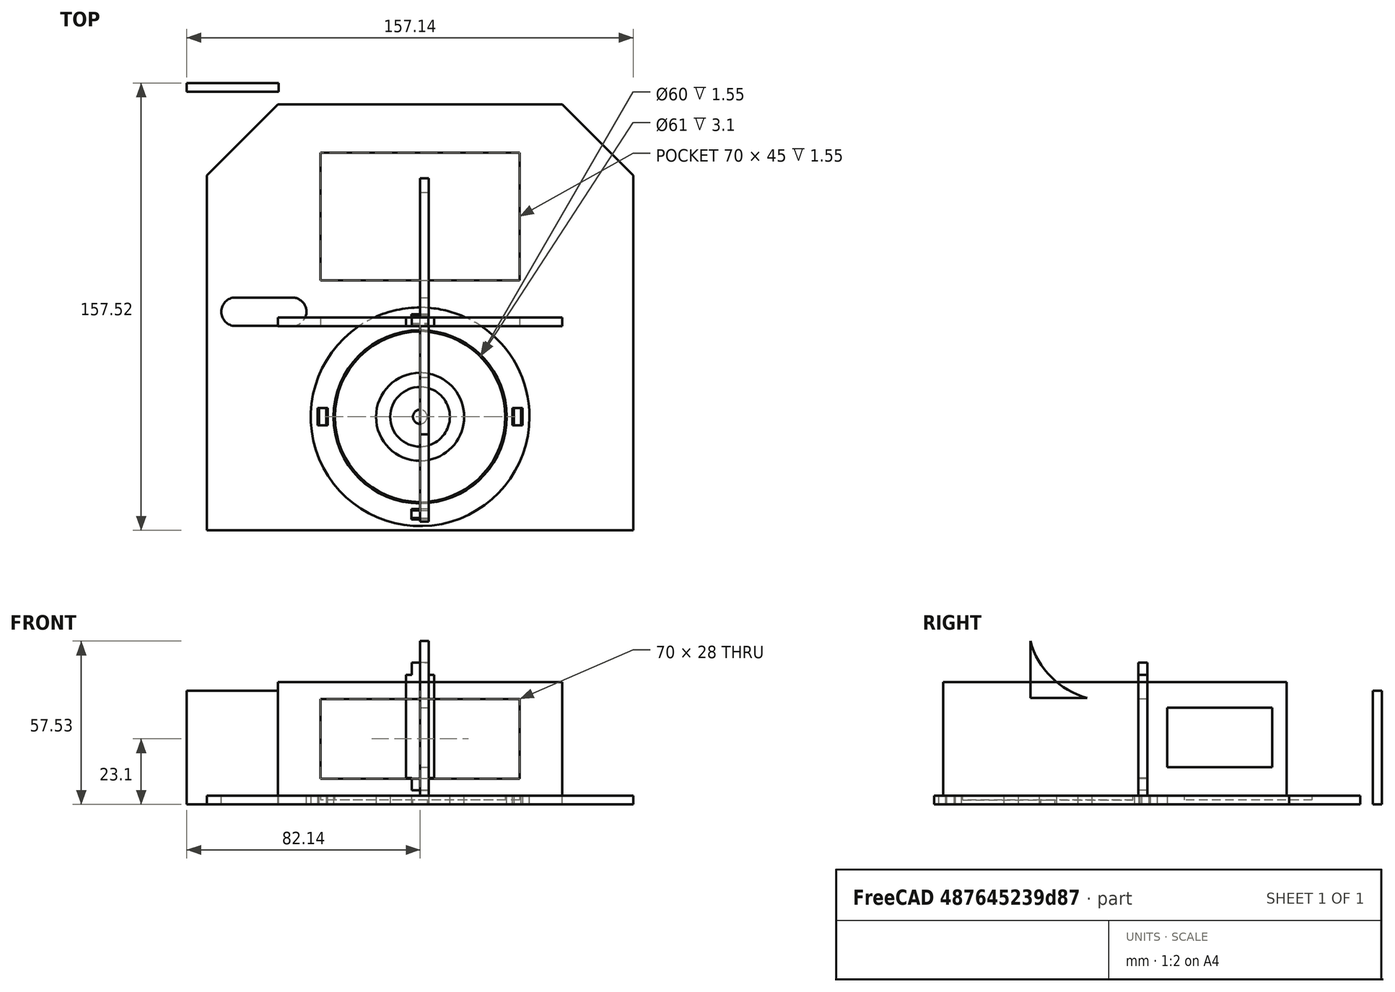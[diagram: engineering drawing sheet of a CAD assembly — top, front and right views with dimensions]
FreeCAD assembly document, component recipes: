
FREECAD ASSEMBLY — COMPONENT RECIPES ("Vehicle_project_3")

This assembly document has 15 components, labeled P0..P14 below (a component is one placed body or linked part). 13 of them carry a construction recipe — the FreeCAD feature program that regenerates the part from scratch, quoted from this document or its linked companion documents; the rest are supplied as boundary geometry only. No exploded tour is included for this assembly.
COMPONENT P0 — geometry summary ("Slice.003"; no construction recipe available for this part):
  bounding box: 150.0 x 105.5 x 72.3 mm
  tessellated surface: 1,640 triangles
  volume: 46763 mm^3 (4% of its bounding box)
COMPONENT P1 — geometry summary ("Slice.002"; no construction recipe available for this part):
  bounding box: 150.0 x 25.0 x 3.1 mm
  tessellated surface: 12 triangles
  volume: 10656 mm^3 (92% of its bounding box)
  symmetry: mirror-symmetric across its z mid-plane
COMPONENT P2 — recipe-attached ("back_side001", modeled in this document).
Construction recipe (the document's own serialized feature program — sketch geometry with constraints, then the solid features built on it; lengths are millimeters unless a unit is written):

FEATURE [Sketcher::SketchObject] Sketch005
  ArcFitTolerance = 1e-06
  AttachmentSupport = -> [XZ_Plane001]
  FullyConstrained = true
  MakeInternals = false
  MapMode = 5
  Placement = pos=(0,0,0) rot=(1,0,0;1.5708rad)
  expr: Constraints[10] = <<dimensions>>.material_thickness
  expr: Constraints[7] = <<dimensions>>.base_width
  expr: Constraints[8] = <<dimensions>>.base_height
  sketch-geometry (4):
    g0: LineSegment StartX=-75 StartY=43.1 StartZ=0 EndX=-75 EndY=3.1 EndZ=0
    g1: LineSegment StartX=-75 StartY=3.1 StartZ=0 EndX=75 EndY=3.1 EndZ=0
    g2: LineSegment StartX=75 StartY=3.1 StartZ=0 EndX=75 EndY=43.1 EndZ=0
    g3: LineSegment StartX=75 StartY=43.1 StartZ=0 EndX=-75 EndY=43.1 EndZ=0
  constraints (11):
    c: Vertical(g0)
    c: Coincident(g0,g1)
    c: Horizontal(g1)
    c: Coincident(g1,g2)
    c: Coincident(g2,g3)
    c: Coincident(g3,g0)
    c: Vertical(g2)
    c: DistanceX(g3,g3) = 150
    c: DistanceY(g2,g2) = 40
    c: Symmetric(g0,g2,g-2)
    c: Distance(g-1,g1) = 3.1
FEATURE [PartDesign::Pad] Pad001
  Direction = (0,-1,2e-16)
  Length = 3.1
  Length2 = 10
  Placement = pos=(0,0,0) rot=(1,0,0;1.5708rad)
  Profile = -> Sketch005
  ReferenceAxis = -> Sketch005 [N_Axis]
  Refine = true
  Suppressed = false
  Type = 0
  expr: Length = <<dimensions>>.material_thickness
FEATURE [Sketcher::SketchObject] Sketch006
  ArcFitTolerance = 1e-06
  AttachmentSupport = -> [Pad001]
  ExternalGeometry = -> [Pad001]
  FullyConstrained = true
  MakeInternals = false
  MapMode = 5
  Placement = pos=(0,-3.1,0) rot=(1,0,0;1.5708rad)
  expr: Constraints[8] = <<dimensions>>.material_thickness + 5 mm
  sketch-geometry (4):
    g0: LineSegment StartX=-66.9 StartY=18.1 StartZ=0 EndX=-66.9 EndY=6.1 EndZ=0
    g1: LineSegment StartX=-66.9 StartY=6.1 StartZ=0 EndX=-51.9 EndY=6.1 EndZ=0
    g2: LineSegment StartX=-51.9 StartY=6.1 StartZ=0 EndX=-51.9 EndY=18.1 EndZ=0
    g3: LineSegment StartX=-51.9 StartY=18.1 StartZ=0 EndX=-66.9 EndY=18.1 EndZ=0
  constraints (12):
    c: Coincident(g0,g1)
    c: Horizontal(g1)
    c: Coincident(g1,g2)
    c: Coincident(g2,g3)
    c: Coincident(g3,g0)
    c: Horizontal(g3)
    c: Vertical(g2)
    c: Vertical(g0)
    c: Distance(g-3,g0) = 8.1
    c: Distance(g-4,g1) = 3
    c: DistanceY(g0,g0) = 12
    c: DistanceX(g1,g1) = 15
FEATURE [PartDesign::Pocket] Pocket004
  BaseFeature = -> Pad001
  Direction = (0,1,-2e-16)
  Length = 5
  Length2 = 5
  Placement = pos=(0,0,0) rot=(1,0,0;1.5708rad)
  Profile = -> Sketch006
  ReferenceAxis = -> Sketch006 [N_Axis]
  Refine = true
  Suppressed = false
  Type = 1
FEATURE [PartDesign::Fillet] Fillet001
  Base = -> Pocket004 [Edge23,Edge22,Edge21,Edge24]
  BaseFeature = -> Pocket004
  Placement = pos=(0,0,0) rot=(1,0,0;1.5708rad)
  Radius = 2
  Refine = true
  SupportTransform = false
  Suppressed = false
  UseAllEdges = false
FEATURE [PartDesign::Body] Body001  label="back_side"
  AllowCompound = false
  Group = -> [Sketch005,Pad001,Sketch006,Pocket004,Fillet001]
  Origin = -> Origin001
  Tip = -> Fillet001
COMPONENT P3 — recipe-attached ("base001", modeled in this document).
Construction recipe (the document's own serialized feature program — sketch geometry with constraints, then the solid features built on it; lengths are millimeters unless a unit is written):

FEATURE [Sketcher::SketchObject] Sketch
  ArcFitTolerance = 1e-06
  AttachmentSupport = -> [XY_Plane]
  FullyConstrained = true
  MakeInternals = false
  MapMode = 5
  expr: Constraints[11] = <<dimensions>>.base_width
  expr: Constraints[12] = <<dimensions>>.base_length
  expr: Constraints[14] = <<dimensions>>.base_length / 2
  expr: Constraints[15] = <<dimensions>>.base_short_side
  expr: Constraints[16] = <<dimensions>>.base_short_side
  sketch-geometry (6):
    g0: LineSegment StartX=-75 StartY=50 StartZ=0 EndX=-75 EndY=-75 EndZ=0
    g1: LineSegment StartX=-75 StartY=-75 StartZ=0 EndX=75 EndY=-75 EndZ=0
    g2: LineSegment StartX=75 StartY=-75 StartZ=0 EndX=75 EndY=50 EndZ=0
    g3: LineSegment StartX=75 StartY=50 StartZ=0 EndX=50 EndY=75 EndZ=0
    g4: LineSegment StartX=50 StartY=75 StartZ=0 EndX=-50 EndY=75 EndZ=0
    g5: LineSegment StartX=-50 StartY=75 StartZ=0 EndX=-75 EndY=50 EndZ=0
  constraints (17):
    c: Vertical(g0)
    c: Coincident(g0,g1)
    c: Horizontal(g1)
    c: Coincident(g1,g2)
    c: Vertical(g2)
    c: Coincident(g2,g3)
    c: Coincident(g3,g4)
    c: Horizontal(g4)
    c: Coincident(g4,g5)
    c: Coincident(g5,g0)
    c: Equal(g5,g3)
    c: DistanceX(g1,g1) = 150
    c: Distance(g1,g4) = 150
    c: Symmetric(g0,g2,g-2)
    c: Distance(g-1,g1) = 75
    c: DistanceY(g0,g4) = 25
    c: DistanceX(g0,g4) = 25
FEATURE [PartDesign::Pad] Pad
  Direction = (0,0,1)
  Length = 3.1
  Length2 = 10
  Profile = -> Sketch
  ReferenceAxis = -> Sketch [N_Axis]
  Refine = true
  Suppressed = false
  Type = 0
  expr: Length = <<dimensions>>.material_thickness
FEATURE [Sketcher::SketchObject] Sketch001
  ArcFitTolerance = 1e-06
  AttachmentSupport = -> [Pad]
  ExternalGeometry = -> [Pad]
  FullyConstrained = true
  MakeInternals = false
  MapMode = 5
  Placement = pos=(0,0,3.1) rot=(0,0,1;0rad)
  expr: Constraints[10] = <<dimensions>>.material_thickness + <<dimensions>>.hole_margin
  expr: Constraints[11] = <<dimensions>>.material_thickness + <<dimensions>>.hole_margin
  expr: Constraints[8] = <<dimensions>>.raspberry_width
  expr: Constraints[9] = <<dimensions>>.raspberry_length
  sketch-geometry (4):
    g0: LineSegment StartX=-70.9 StartY=-9.9 StartZ=0 EndX=-70.9 EndY=-70.9 EndZ=0
    g1: LineSegment StartX=-70.9 StartY=-70.9 StartZ=0 EndX=18.1 EndY=-70.9 EndZ=0
    g2: LineSegment StartX=18.1 StartY=-70.9 StartZ=0 EndX=18.1 EndY=-9.9 EndZ=0
    g3: LineSegment StartX=18.1 StartY=-9.9 StartZ=0 EndX=-70.9 EndY=-9.9 EndZ=0
  constraints (12):
    c: Vertical(g0)
    c: Coincident(g0,g1)
    c: Coincident(g1,g2)
    c: Coincident(g2,g3)
    c: Coincident(g3,g0)
    c: Horizontal(g0,g2)
    c: Horizontal(g1,g0)
    c: Vertical(g2)
    c: DistanceX(g3,g3) = 89
    c: DistanceY(g2,g2) = 61
    c: Distance(g-3,g0) = 4.1
    c: Distance(g1,g-4) = 4.1
FEATURE [PartDesign::Pocket] Pocket
  BaseFeature = -> Pad
  Direction = (0,0,-1)
  Length = 1.55
  Length2 = 5
  Profile = -> Sketch001
  ReferenceAxis = -> Sketch001 [N_Axis]
  Refine = true
  Suppressed = false
  Type = 0
  expr: Length = <<dimensions>>.material_thickness / 2
FEATURE [Sketcher::SketchObject] Sketch002
  ArcFitTolerance = 1e-06
  AttachmentSupport = -> [Pocket]
  ExternalGeometry = -> [Pocket]
  FullyConstrained = true
  MakeInternals = false
  MapMode = 5
  Placement = pos=(0,0,3.1) rot=(0,0,1;0rad)
  sketch-geometry (4):
    g0: LineSegment StartX=-70.9 StartY=46.8875 StartZ=0 EndX=-70.9 EndY=-3.11249 EndZ=0
    g1: LineSegment StartX=-70.9 StartY=-3.11249 StartZ=0 EndX=9.1 EndY=-3.11249 EndZ=0
    g2: LineSegment StartX=9.1 StartY=-3.11249 StartZ=0 EndX=9.1 EndY=46.8875 EndZ=0
    g3: LineSegment StartX=9.1 StartY=46.8875 StartZ=0 EndX=-70.9 EndY=46.8875 EndZ=0
  constraints (12):
    c: Coincident(g0,g1)
    c: Coincident(g1,g2)
    c: Coincident(g2,g3)
    c: Coincident(g3,g0)
    c: Horizontal(g3)
    c: Horizontal(g1)
    c: Vertical(g2)
    c: Vertical(g0)
    c: DistanceX(g3,g3) = 80  '=di'
    c: DistanceY(g0,g0) = 50
    c: Vertical(g0,g-4)
    c: Distance(g0,g-6) = 5.1
FEATURE [PartDesign::Pocket] Pocket001
  BaseFeature = -> Pocket
  Direction = (0,0,-1)
  Length = 1.55
  Length2 = 5
  Profile = -> Sketch002
  ReferenceAxis = -> Sketch002 [N_Axis]
  Refine = true
  Suppressed = false
  Type = 0
  expr: Length = <<dimensions>>.material_thickness / 2
FEATURE [Sketcher::SketchObject] Sketch003
  ArcFitTolerance = 1e-06
  AttachmentSupport = -> [Pocket001]
  ExternalGeometry = -> [Pocket001]
  FullyConstrained = true
  MakeInternals = false
  MapMode = 5
  Placement = pos=(0,0,3.1) rot=(0,0,1;0rad)
  expr: Constraints[9] = <<dimensions>>.material_thickness + 3 mm
  sketch-geometry (4):
    g0: LineSegment StartX=45 StartY=-61.9 StartZ=0 EndX=45 EndY=-68.9 EndZ=0
    g1: LineSegment StartX=45 StartY=-68.9 StartZ=0 EndX=60 EndY=-68.9 EndZ=0
    g2: LineSegment StartX=60 StartY=-68.9 StartZ=0 EndX=60 EndY=-61.9 EndZ=0
    g3: LineSegment StartX=60 StartY=-61.9 StartZ=0 EndX=45 EndY=-61.9 EndZ=0
  constraints (12):
    c: Coincident(g0,g1)
    c: Coincident(g1,g2)
    c: Coincident(g2,g3)
    c: Coincident(g3,g0)
    c: Horizontal(g3)
    c: Horizontal(g1)
    c: Vertical(g0)
    c: Vertical(g2)
    c: Distance(g-3,g2) = 15
    c: Distance(g-4,g1) = 6.1
    c: DistanceY(g2,g2) = 7
    c: DistanceX(g3,g3) = 15
FEATURE [PartDesign::Pocket] Pocket002
  BaseFeature = -> Pocket001
  Direction = (0,0,-1)
  Length = 5
  Length2 = 5
  Profile = -> Sketch003
  ReferenceAxis = -> Sketch003 [N_Axis]
  Refine = true
  Suppressed = false
  Type = 1
FEATURE [PartDesign::Fillet] Fillet
  Base = -> Pocket002 [Edge36,Edge38,Edge35,Edge37]
  BaseFeature = -> Pocket002
  Radius = 3
  Refine = true
  SupportTransform = false
  Suppressed = false
  UseAllEdges = false
FEATURE [Sketcher::SketchObject] Sketch004
  ArcFitTolerance = 1e-06
  AttachmentSupport = -> [Fillet]
  ExternalGeometry = -> [Fillet]
  FullyConstrained = true
  MakeInternals = false
  MapMode = 5
  Placement = pos=(0,0,3.1) rot=(0,0,1;0rad)
  expr: Constraints[8] = <<dimensions>>.bridge_side
  expr: Constraints[9] = <<dimensions>>.bridge_side
  sketch-geometry (4):
    g0: LineSegment StartX=19.1 StartY=46.8875 StartZ=0 EndX=19.1 EndY=1.88751 EndZ=0
    g1: LineSegment StartX=19.1 StartY=1.88751 StartZ=0 EndX=64.1 EndY=1.88751 EndZ=0
    g2: LineSegment StartX=64.1 StartY=1.88751 StartZ=0 EndX=64.1 EndY=46.8875 EndZ=0
    g3: LineSegment StartX=64.1 StartY=46.8875 StartZ=0 EndX=19.1 EndY=46.8875 EndZ=0
  constraints (12):
    c: Vertical(g0)
    c: Coincident(g0,g1)
    c: Coincident(g1,g2)
    c: Coincident(g2,g3)
    c: Coincident(g3,g0)
    c: Horizontal(g3)
    c: Vertical(g2)
    c: Horizontal(g1)
    c: DistanceY(g2,g2) = 45
    c: DistanceX(g3,g3) = 45
    c: Distance(g-3,g0) = 10
    c: Horizontal(g-3,g0)
FEATURE [PartDesign::Pocket] Pocket003
  BaseFeature = -> Fillet
  Direction = (0,0,-1)
  Length = 1.55
  Length2 = 5
  Profile = -> Sketch004
  ReferenceAxis = -> Sketch004 [N_Axis]
  Refine = true
  Suppressed = false
  Type = 0
  expr: Length = <<dimensions>>.material_thickness / 2
FEATURE [Sketcher::SketchObject] Sketch028
  ArcFitTolerance = 1e-06
  AttachmentSupport = -> [Pocket003]
  ExternalGeometry = -> [Pocket003]
  FullyConstrained = true
  MakeInternals = false
  MapMode = 5
  Placement = pos=(0,0,3.1) rot=(0,0,1;0rad)
  expr: Constraints[10] = <<dimensions>>.material_thickness + <<dimensions>>.hole_margin
  sketch-geometry (4):
    g0: LineSegment StartX=28.1 StartY=-5.11249 StartZ=0 EndX=28.1 EndY=-53.9 EndZ=0
    g1: LineSegment StartX=28.1 StartY=-53.9 StartZ=0 EndX=70.9 EndY=-53.9 EndZ=0
    g2: LineSegment StartX=70.9 StartY=-53.9 StartZ=0 EndX=70.9 EndY=-5.11249 EndZ=0
    g3: LineSegment StartX=70.9 StartY=-5.11249 StartZ=0 EndX=28.1 EndY=-5.11249 EndZ=0
  constraints (12):
    c: Vertical(g0)
    c: Coincident(g0,g1)
    c: Horizontal(g1)
    c: Coincident(g1,g2)
    c: Coincident(g2,g3)
    c: Coincident(g3,g0)
    c: Horizontal(g3)
    c: Distance(g-4,g1) = 8
    c: Vertical(g2)
    c: Distance(g3,g-7) = 7
    c: Distance(g-6,g2) = 4.1
    c: Distance(g-5,g0) = 10
FEATURE [PartDesign::Pocket] Pocket016
  BaseFeature = -> Pocket003
  Direction = (0,0,-1)
  Length = 1.55
  Length2 = 5
  Profile = -> Sketch028
  ReferenceAxis = -> Sketch028 [N_Axis]
  Refine = true
  Suppressed = false
  Type = 0
  expr: Length = <<dimensions>>.material_thickness / 2
FEATURE [PartDesign::Body] Body  label="base"
  AllowCompound = false
  Group = -> [Sketch,Pad,Sketch001,Pocket,Sketch002,Pocket001,Sketch003,Pocket002,Fillet,Sketch004,Pocket003,Sketch028,Pocket016]
  Origin = -> Origin
  Tip = -> Pocket016
COMPONENT P4 — recipe-attached ("cup_holder_top001", modeled in this document).
Construction recipe (the document's own serialized feature program — sketch geometry with constraints, then the solid features built on it; lengths are millimeters unless a unit is written):

FEATURE [Sketcher::SketchObject] Sketch029
  ArcFitTolerance = 1e-06
  AttachmentSupport = -> [XY_Plane013]
  FullyConstrained = false
  MakeInternals = false
  MapMode = 5
  expr: Constraints[13] = <<dimensions>>.material_thickness
  expr: Constraints[14] = <<dimensions>>.material_thickness + 3 mm
  expr: Constraints[36] = <<dimensions>>.material_thickness + 3 mm
  expr: Constraints[37] = <<dimensions>>.material_thickness
  sketch-geometry (20):
    g0: Circle CenterX=0 CenterY=-35 CenterZ=0 NormalX=0 NormalY=0 NormalZ=1 AngleXU=0 Radius=30.5
    g1: Circle CenterX=0 CenterY=-35 CenterZ=0 NormalX=0 NormalY=0 NormalZ=1 AngleXU=0 Radius=38.5
    g2: LineSegment StartX=-35.6 StartY=-31.95 StartZ=0 EndX=-35.6 EndY=-38.05 EndZ=0
    g3: LineSegment StartX=-35.6 StartY=-38.05 StartZ=0 EndX=-32.5 EndY=-38.05 EndZ=0
    g4: LineSegment StartX=-32.5 StartY=-38.05 StartZ=0 EndX=-32.5 EndY=-31.95 EndZ=0
    g5: LineSegment StartX=-32.5 StartY=-31.95 StartZ=0 EndX=-35.6 EndY=-31.95 EndZ=0
    g6: LineSegment [constr] StartX=0 StartY=-35 StartZ=0 EndX=-58.4868 EndY=-35 EndZ=0
    g7: LineSegment [constr] StartX=0 StartY=-35 StartZ=0 EndX=54.8346 EndY=-35 EndZ=0
    g8: LineSegment StartX=32.5 StartY=-31.95 StartZ=0 EndX=32.5 EndY=-38.05 EndZ=0
    g9: LineSegment StartX=32.5 StartY=-38.05 StartZ=0 EndX=35.6 EndY=-38.05 EndZ=0
    g10: LineSegment StartX=35.6 StartY=-38.05 StartZ=0 EndX=35.6 EndY=-31.95 EndZ=0
    g11: LineSegment StartX=35.6 StartY=-31.95 StartZ=0 EndX=32.5 EndY=-31.95 EndZ=0
    g12: LineSegment StartX=-3.05 StartY=0.6 StartZ=0 EndX=-3.05 EndY=-2.5 EndZ=0
    g13: LineSegment StartX=-3.05 StartY=-2.5 StartZ=0 EndX=3.05 EndY=-2.5 EndZ=0
    g14: LineSegment StartX=3.05 StartY=-2.5 StartZ=0 EndX=3.05 EndY=0.6 EndZ=0
    g15: LineSegment StartX=3.05 StartY=0.6 StartZ=0 EndX=-3.05 EndY=0.6 EndZ=0
    g16: LineSegment StartX=-3.05 StartY=-67.5 StartZ=0 EndX=-3.05 EndY=-70.6 EndZ=0
    g17: LineSegment StartX=-3.05 StartY=-70.6 StartZ=0 EndX=3.05 EndY=-70.6 EndZ=0
    g18: LineSegment StartX=3.05 StartY=-70.6 StartZ=0 EndX=3.05 EndY=-67.5 EndZ=0
    g19: LineSegment StartX=3.05 StartY=-67.5 StartZ=0 EndX=-3.05 EndY=-67.5 EndZ=0
  constraints (49):
    c: Diameter(g0) = 61
    c: PointOnObject(g0,g-2)
    c: Coincident(g1,g0)
    c: Distance(g0,g1) = 8
    c: Distance(g0,g-1) = 35
    c: Coincident(g2,g3)
    c: Coincident(g3,g4)
    c: Coincident(g4,g5)
    c: Coincident(g5,g2)
    c: Vertical(g2)
    c: Vertical(g4)
    c: Horizontal(g3)
    c: Horizontal(g5)
    c: DistanceX(g5,g5) = 3.1
    c: DistanceY(g2,g2) = 6.1
    c: Distance(g0,g4) = 2
    c: Coincident(g6,g0)
    c: Coincident(g7,g0)
    c: Horizontal(g7)
    c: Symmetric(g4,g3,g6)
    c: Coincident(g8,g9)
    c: Coincident(g9,g10)
    c: Coincident(g10,g11)
    c: Coincident(g11,g8)
    c: Vertical(g10)
    c: Horizontal(g11)
    c: Symmetric(g4,g8,g0)
    c: Symmetric(g3,g8,g0)
    c: Symmetric(g2,g9,g0)
    c: Coincident(g12,g13)
    c: Coincident(g13,g14)
    c: Coincident(g14,g15)
    c: Coincident(g15,g12)
    c: Vertical(g12)
    c: Vertical(g14)
    c: Horizontal(g13)
    c: DistanceX(g13,g13) = 6.1
    c: DistanceY(g14,g14) = 3.1
    c: Distance(g0,g13) = 2
    c: Symmetric(g12,g14,g-2)
    c: Coincident(g16,g17)
    c: Coincident(g17,g18)
    c: Coincident(g18,g19)
    c: Coincident(g19,g16)
    c: Vertical(g16)
    c: Horizontal(g17)
    c: Symmetric(g12,g18,g0)
    c: Symmetric(g13,g16,g0)
    c: Symmetric(g12,g17,g0)
FEATURE [PartDesign::Pad] Pad011
  Direction = (0,0,1)
  Length = 3.1
  Length2 = 10
  Profile = -> Sketch029
  ReferenceAxis = -> Sketch029 [N_Axis]
  Refine = true
  Suppressed = false
  Type = 0
  expr: Length = <<dimensions>>.material_thickness
FEATURE [PartDesign::Body] Body011  label="cup_holder_top"
  AllowCompound = false
  Group = -> [Sketch029,Pad011]
  Origin = -> Origin013
  Tip = -> Pad011
COMPONENT P5 — recipe-attached ("cup_holder_vertical001", modeled in this document).
Construction recipe (the document's own serialized feature program — sketch geometry with constraints, then the solid features built on it; lengths are millimeters unless a unit is written):

FEATURE [Sketcher::SketchObject] Sketch017
  ArcFitTolerance = 1e-06
  AttachmentSupport = -> [XZ_Plane008]
  FullyConstrained = true
  MakeInternals = false
  MapMode = 5
  Placement = pos=(0,0,0) rot=(1,0,0;1.5708rad)
  expr: Constraints[19] = (<<dimensions>>.material_thickness + 3 mm) / 2 * 0.95
  sketch-geometry (8):
    g0: LineSegment StartX=0 StartY=5 StartZ=0 EndX=2.8975 EndY=5 EndZ=0
    g1: LineSegment StartX=2.8975 StartY=5 StartZ=0 EndX=2.8975 EndY=9.33 EndZ=0
    g2: LineSegment StartX=2.8975 StartY=9.33 StartZ=0 EndX=5 EndY=9.33 EndZ=0
    g3: LineSegment StartX=5 StartY=9.33 StartZ=0 EndX=5 EndY=45.67 EndZ=0
    g4: LineSegment StartX=5 StartY=45.67 StartZ=0 EndX=2.8975 EndY=45.67 EndZ=0
    g5: LineSegment StartX=2.8975 StartY=45.67 StartZ=0 EndX=2.8975 EndY=50 EndZ=0
    g6: LineSegment StartX=2.8975 StartY=50 StartZ=0 EndX=0 EndY=50 EndZ=0
    g7: LineSegment StartX=0 StartY=50 StartZ=0 EndX=0 EndY=5 EndZ=0
  constraints (24):
    c: PointOnObject(g0,g-2)
    c: Horizontal(g0)
    c: Coincident(g0,g1)
    c: Vertical(g1)
    c: Coincident(g1,g2)
    c: Horizontal(g2)
    c: Coincident(g2,g3)
    c: Vertical(g3)
    c: Coincident(g3,g4)
    c: Horizontal(g4)
    c: Coincident(g4,g5)
    c: Vertical(g5)
    c: Coincident(g5,g6)
    c: PointOnObject(g6,g-2)
    c: Coincident(g6,g7)
    c: Coincident(g7,g0)
    c: Horizontal(g6)
    c: Equal(g5,g1)
    c: DistanceY(g1,g1) = 4.33
    c: DistanceX(g0,g0) = 2.8975
    c: Equal(g6,g0)
    c: Distance(g6,g0) = 45
    c: Distance(g7,g3) = 5
    c: Distance(g0,g-1) = 5
FEATURE [PartDesign::Pad] Pad007
  Direction = (0,-1,2e-16)
  Length = 3.1
  Length2 = 10
  Placement = pos=(0,0,0) rot=(1,0,0;1.5708rad)
  Profile = -> Sketch017
  ReferenceAxis = -> Sketch017 [N_Axis]
  Refine = true
  Suppressed = false
  Type = 0
  expr: Length = <<dimensions>>.material_thickness
FEATURE [PartDesign::Mirrored] Mirrored001
  BaseFeature = -> Pad007
  MirrorPlane = -> Sketch017 [V_Axis]
  Originals = -> [Pad007]
  Placement = pos=(0,0,0) rot=(1,0,0;1.5708rad)
  Refine = true
  Suppressed = false
  TransformMode = 0
FEATURE [PartDesign::Body] Body007  label="cup_holder_vertical"
  AllowCompound = false
  Group = -> [Sketch017,Pad007,Mirrored001]
  Origin = -> Origin008
  Tip = -> Mirrored001
COMPONENT P6 — same part as P5; its construction recipe is shown at P5.
COMPONENT P7 — same part as P5; its construction recipe is shown at P5.
COMPONENT P8 — same part as P5; its construction recipe is shown at P5.
COMPONENT P9 — recipe-attached ("front_angle_side001", modeled in this document).
Construction recipe (the document's own serialized feature program — sketch geometry with constraints, then the solid features built on it; lengths are millimeters unless a unit is written):

FEATURE [Sketcher::SketchObject] Sketch010
  ArcFitTolerance = 1e-06
  AttachmentSupport = -> [XY_Plane004]
  FullyConstrained = false
  MakeInternals = false
  MapMode = 5
  expr: Constraints[8] = sqrt(1250) - 3
  expr: Constraints[9] = <<dimensions>>.material_thickness
  sketch-geometry (4):
    g0: LineSegment StartX=-82.1409 StartY=82.5247 StartZ=0 EndX=-49.7856 EndY=82.5247 EndZ=0
    g1: LineSegment StartX=-49.7856 StartY=82.5247 StartZ=0 EndX=-49.7856 EndY=79.4247 EndZ=0
    g2: LineSegment StartX=-49.7856 StartY=79.4247 StartZ=0 EndX=-82.1409 EndY=79.4247 EndZ=0
    g3: LineSegment StartX=-82.1409 StartY=79.4247 StartZ=0 EndX=-82.1409 EndY=82.5247 EndZ=0
  constraints (10):
    c: Horizontal(g0)
    c: Coincident(g0,g1)
    c: Coincident(g1,g2)
    c: Horizontal(g2)
    c: Coincident(g2,g3)
    c: Coincident(g3,g0)
    c: Vertical(g3)
    c: Vertical(g1)
    c: DistanceX(g0,g0) = 32.3553
    c: DistanceY(g1,g1) = 3.1
FEATURE [PartDesign::Pad] Pad004
  Direction = (0,0,1)
  Length = 40
  Length2 = 10
  Profile = -> Sketch010
  ReferenceAxis = -> Sketch010 [N_Axis]
  Refine = true
  Suppressed = false
  Type = 0
  expr: Length = <<dimensions>>.base_height
FEATURE [PartDesign::Body] Body004  label="front_angle_side"
  AllowCompound = false
  Group = -> [Sketch010,Pad004]
  Origin = -> Origin004
  Tip = -> Pad004
COMPONENT P10 — same part as P9; its construction recipe is shown at P9.
COMPONENT P11 — recipe-attached ("front_side001", modeled in this document).
Construction recipe (the document's own serialized feature program — sketch geometry with constraints, then the solid features built on it; lengths are millimeters unless a unit is written):

FEATURE [Sketcher::SketchObject] Sketch011
  ArcFitTolerance = 1e-06
  AttachmentSupport = -> [XZ_Plane005]
  FullyConstrained = true
  MakeInternals = false
  MapMode = 5
  Placement = pos=(0,0,0) rot=(1,0,0;1.5708rad)
  expr: Constraints[15] = <<dimensions>>.base_width / 2 - 25 mm
  expr: Constraints[18] = <<dimensions>>.material_thickness
  expr: Constraints[23] = <<dimensions>>.base_height
  sketch-geometry (8):
    g0: LineSegment StartX=0 StartY=43.1 StartZ=0 EndX=0 EndY=37.1 EndZ=0
    g1: LineSegment StartX=-35 StartY=37.1 StartZ=0 EndX=-35 EndY=9.1 EndZ=0
    g2: LineSegment StartX=-35 StartY=9.1 StartZ=0 EndX=0 EndY=9.1 EndZ=0
    g3: LineSegment StartX=0 StartY=9.1 StartZ=0 EndX=0 EndY=3.1 EndZ=0
    g4: LineSegment StartX=0 StartY=3.1 StartZ=0 EndX=-50 EndY=3.1 EndZ=0
    g5: LineSegment StartX=-50 StartY=3.1 StartZ=0 EndX=-50 EndY=43.1 EndZ=0
    g6: LineSegment StartX=-50 StartY=43.1 StartZ=0 EndX=0 EndY=43.1 EndZ=0
    g7: LineSegment StartX=0 StartY=37.1 StartZ=0 EndX=-35 EndY=37.1 EndZ=0
  constraints (24):
    c: PointOnObject(g0,g-2)
    c: PointOnObject(g0,g-2)
    c: Vertical(g1)
    c: Coincident(g1,g2)
    c: PointOnObject(g2,g-2)
    c: Horizontal(g2)
    c: Coincident(g2,g3)
    c: PointOnObject(g3,g-2)
    c: Coincident(g3,g4)
    c: Horizontal(g4)
    c: Coincident(g4,g5)
    c: Vertical(g5)
    c: Coincident(g5,g6)
    c: Coincident(g6,g0)
    c: Horizontal(g6)
    c: DistanceX(g4,g4) = 50
    c: Distance(g4,g2) = 6
    c: Distance(g5,g1) = 15
    c: Distance(g-1,g4) = 3.1
    c: Coincident(g0,g7)
    c: Coincident(g7,g1)
    c: Horizontal(g7)
    c: Distance(g6,g7) = 6
    c: DistanceY(g5,g5) = 40
FEATURE [PartDesign::Pad] Pad005
  Direction = (0,-1,2e-16)
  Length = 3.1
  Length2 = 10
  Placement = pos=(0,0,0) rot=(1,0,0;1.5708rad)
  Profile = -> Sketch011
  ReferenceAxis = -> Sketch011 [N_Axis]
  Refine = true
  Suppressed = false
  Type = 0
  expr: Length = <<dimensions>>.material_thickness
FEATURE [PartDesign::Mirrored] Mirrored
  BaseFeature = -> Pad005
  MirrorPlane = -> YZ_Plane005
  Placement = pos=(0,0,0) rot=(1,0,0;1.5708rad)
  Refine = true
  Suppressed = false
  TransformMode = 1
FEATURE [PartDesign::Body] Body005  label="front_side"
  AllowCompound = false
  Group = -> [Sketch011,Pad005,Mirrored]
  Origin = -> Origin005
  Tip = -> Mirrored
COMPONENT P12 — recipe-attached ("left_side001", modeled in this document).
Construction recipe (the document's own serialized feature program — sketch geometry with constraints, then the solid features built on it; lengths are millimeters unless a unit is written):

FEATURE [Sketcher::SketchObject] Sketch008
  ArcFitTolerance = 1e-06
  AttachmentSupport = -> [YZ_Plane003]
  FullyConstrained = true
  MakeInternals = false
  MapMode = 5
  Placement = pos=(0,0,0) rot=(0.57735,0.57735,0.57735;2.0944rad)
  sketch-geometry (4):
    g0: LineSegment StartX=-71.9 StartY=43.1 StartZ=0 EndX=-71.9 EndY=3.1 EndZ=0
    g1: LineSegment StartX=-71.9 StartY=3.1 StartZ=0 EndX=49 EndY=3.1 EndZ=0
    g2: LineSegment StartX=-71.9 StartY=43.1 StartZ=0 EndX=49 EndY=43.1 EndZ=0
    g3: LineSegment StartX=49 StartY=43.1 StartZ=0 EndX=49 EndY=3.1 EndZ=0
  constraints (12):
    c: Coincident(g0,g1)
    c: Horizontal(g1)
    c: Coincident(g0,g2)
    c: Coincident(g2,g3)
    c: Coincident(g3,g1)
    c: Vertical(g3)
    c: Horizontal(g2)
    c: Vertical(g0)
    c: DistanceY(g0,g0) = 40
    c: DistanceX(g1,g1) = 120.9
    c: Distance(g-2,g0) = 71.9
    c: Distance(g-1,g1) = 3.1
FEATURE [PartDesign::Pad] Pad003
  Direction = (1,0,0)
  Length = 3.1
  Length2 = 10
  Placement = pos=(0,0,0) rot=(1,1,1;2.0944rad)
  Profile = -> Sketch008
  ReferenceAxis = -> Sketch008 [N_Axis]
  Refine = true
  Suppressed = false
  Type = 0
  expr: Length = <<dimensions>>.material_thickness
FEATURE [Sketcher::SketchObject] Sketch009
  ArcFitTolerance = 1e-06
  AttachmentSupport = -> [Pad003]
  ExternalGeometry = -> [Pad003]
  FullyConstrained = true
  MakeInternals = false
  MapMode = 5
  Placement = pos=(0,0,0) rot=(0.57735,0.57735,-0.57735;4.18879rad)
  sketch-geometry (4):
    g0: LineSegment StartX=44 StartY=-34.1 StartZ=0 EndX=44 EndY=-13.1 EndZ=0
    g1: LineSegment StartX=44 StartY=-13.1 StartZ=0 EndX=7 EndY=-13.1 EndZ=0
    g2: LineSegment StartX=7 StartY=-13.1 StartZ=0 EndX=7 EndY=-34.1 EndZ=0
    g3: LineSegment StartX=7 StartY=-34.1 StartZ=0 EndX=44 EndY=-34.1 EndZ=0
  constraints (12):
    c: Coincident(g0,g1)
    c: Horizontal(g1)
    c: Coincident(g1,g2)
    c: Coincident(g2,g3)
    c: Coincident(g3,g0)
    c: Horizontal(g3)
    c: Vertical(g0)
    c: Vertical(g2)
    c: Distance(g-4,g0) = 5
    c: Distance(g-3,g3) = 9
    c: DistanceY(g0,g0) = 21
    c: DistanceX(g1,g1) = 37
FEATURE [PartDesign::Pocket] Pocket005
  BaseFeature = -> Pad003
  Direction = (1,0,0)
  Length = 5
  Length2 = 5
  Placement = pos=(0,0,0) rot=(1,1,1;2.0944rad)
  Profile = -> Sketch009
  ReferenceAxis = -> Sketch009 [N_Axis]
  Refine = true
  Suppressed = false
  Type = 1
FEATURE [PartDesign::Body] Body003  label="left_side"
  AllowCompound = false
  Group = -> [Sketch008,Pad003,Sketch009,Pocket005]
  Origin = -> Origin003
  Tip = -> Pocket005
COMPONENT P13 — recipe-attached ("right_side001", modeled in this document).
Construction recipe (the document's own serialized feature program — sketch geometry with constraints, then the solid features built on it; lengths are millimeters unless a unit is written):

FEATURE [Sketcher::SketchObject] Sketch007
  ArcFitTolerance = 1e-06
  AttachmentSupport = -> [YZ_Plane002]
  FullyConstrained = true
  MakeInternals = false
  MapMode = 5
  Placement = pos=(0,0,0) rot=(0.57735,0.57735,0.57735;2.0944rad)
  expr: Constraints[10] = <<dimensions>>.base_length / 2 - <<dimensions>>.material_thickness
  expr: Constraints[11] = <<dimensions>>.material_thickness
  expr: Constraints[8] = <<dimensions>>.base_height
  expr: Constraints[9] = <<dimensions>>.base_length - <<dimensions>>.material_thickness - 26 mm
  sketch-geometry (4):
    g0: LineSegment StartX=-71.9 StartY=43.1 StartZ=0 EndX=-71.9 EndY=3.1 EndZ=0
    g1: LineSegment StartX=-71.9 StartY=3.1 StartZ=0 EndX=49 EndY=3.1 EndZ=0
    g2: LineSegment StartX=-71.9 StartY=43.1 StartZ=0 EndX=49 EndY=43.1 EndZ=0
    g3: LineSegment StartX=49 StartY=43.1 StartZ=0 EndX=49 EndY=3.1 EndZ=0
  constraints (12):
    c: Coincident(g0,g1)
    c: Horizontal(g1)
    c: Coincident(g0,g2)
    c: Coincident(g2,g3)
    c: Coincident(g3,g1)
    c: Vertical(g3)
    c: Horizontal(g2)
    c: Vertical(g0)
    c: DistanceY(g0,g0) = 40
    c: DistanceX(g1,g1) = 120.9
    c: Distance(g-2,g0) = 71.9
    c: Distance(g-1,g1) = 3.1
FEATURE [PartDesign::Pad] Pad002
  Direction = (1,0,0)
  Length = 3.1
  Length2 = 10
  Placement = pos=(0,0,0) rot=(1,1,1;2.0944rad)
  Profile = -> Sketch007
  ReferenceAxis = -> Sketch007 [N_Axis]
  Refine = true
  Suppressed = false
  Type = 0
  expr: Length = <<dimensions>>.material_thickness
FEATURE [PartDesign::Body] Body002  label="right_side"
  AllowCompound = false
  Group = -> [Sketch007,Pad002]
  Origin = -> Origin002
  Tip = -> Pad002
COMPONENT P14 — recipe-attached ("support_ring001", modeled in this document).
Construction recipe (the document's own serialized feature program — sketch geometry with constraints, then the solid features built on it; lengths are millimeters unless a unit is written):

FEATURE [Sketcher::SketchObject] Sketch018
  ArcFitTolerance = 1e-06
  AttachmentSupport = -> [XY_Plane009]
  FullyConstrained = true
  MakeInternals = false
  MapMode = 5
  sketch-geometry (2):
    g0: Circle CenterX=0 CenterY=-35 CenterZ=0 NormalX=0 NormalY=0 NormalZ=1 AngleXU=0 Radius=10.5
    g1: Circle CenterX=0 CenterY=-35 CenterZ=0 NormalX=0 NormalY=0 NormalZ=1 AngleXU=0 Radius=15.5
  constraints (5):
    c: Diameter(g0) = 21
    c: PointOnObject(g0,g-2)
    c: Diameter(g1) = 31
    c: Coincident(g1,g0)
    c: Distance(g0,g-1) = 35
FEATURE [PartDesign::Pad] Pad008
  Direction = (0,0,1)
  Length = 3.1
  Length2 = 10
  Profile = -> Sketch018
  ReferenceAxis = -> Sketch018 [N_Axis]
  Refine = true
  Suppressed = false
  Type = 0
  expr: Length = <<dimensions>>.material_thickness
FEATURE [PartDesign::Body] Body008  label="support_ring"
  AllowCompound = false
  Group = -> [Sketch018,Pad008]
  Origin = -> Origin009
  Tip = -> Pad008
PROVENANCE & LICENSES
A FreeCAD (.FCStd) document from a public repository crawl; recipes are the document's own serialized feature recipes (and, for linked parts, companion documents' recipes).
License: as declared in the source repository (recorded in the dataset sidecar).
